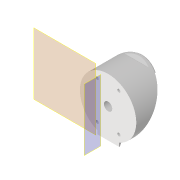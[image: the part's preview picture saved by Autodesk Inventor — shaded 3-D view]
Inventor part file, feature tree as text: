
AUTODESK INVENTOR PART (.ipt)
format: ipt  version: 2022 (Build 260153000, 153)  size: 188,928 bytes
history: native  units: in
note: dims shown in document units (in); Inventor stores cm internally (conversion verified against a paired STEP export)
features: reference x9, other x5, extrude x4, sketch x4, projected_geometry x4, plane x3
ambient origin geometry x8: Origin, YZ Plane, XZ Plane, XY Plane, X Axis, Y Axis, Z Axis, Center Point
bodies: Solid1 (feature_tree)
feature tree (29):
  plane  "Work Plane1"
  plane  "Arbeitsebene5"
  extrude  "Extrusion1"  Depth=0.315in
  extrude  "Extrusion13"  Depth=0.0394in TaperAngle=0.0deg
  plane  "Arbeitsebene6"
  extrude  "Extrusion14"  Depth=0.0197in TaperAngle=0.0deg
  extrude  "Extrusion15"  TaperAngle=90.0deg  [1 undecoded]
  sketch  "Sketch1"  dims[d0=0.1969in d1=0.0in d2=0.315in]
  reference  "Reference1"
  reference  "Reference2"
  reference  "Reference3"
  reference  "Reference4"
  reference  "Reference5"
  reference  "Reference6"
  reference  "Reference7"
  reference  "Reference8"
  sketch  "Skizze17"  dims[d65=0.0079in d66=0.0394in d67=0.0in]
  reference  "Referenz30"
  projected_geometry  "Projizierte Kontur2"
  sketch  "Skizze18"  dims[d68=0.0197in d69=0.7874in d70=0.0in]
  projected_geometry  "Projizierte Kontur3"
  projected_geometry  "Projizierte Kontur4"
  sketch  "Skizze19"  dims[d71=135.0deg d72=90.0deg d73=0.0197in d74=0.0in d75=0.0in]
  projected_geometry  "Projizierte Kontur5"
  other  "Assembly1"
  other  "Assembly_MANATEE_V0_Manatee_middle2_v0_18:1"
  other  "Spectroscope_v0.iam"
  other  "00_Grating_1000linesPerMM:1"
  other  "Matchboxscope_bottom_v0:1"
note: 1 required parameter value undecoded (feature->parameter linkage not recoverable at this tier; creation-order binding heuristic only, values carry confidence <= 0.55)
